# Revit family: BE_84292_de_DE
name_source: partatom
category: Leuchten
units: mm (PartAtom-declared; Revit-internal decimal feet)

## family parameters
Basisbauteil = Fläche
Beim Laden mit Abzugskörper schneiden = Ja
Bemaßung runder Anschluss = Durchmesser verwenden
Gemeinsam genutzt = Nein
Lichtquelle = Ja
Raumberechnungspunkt = Ja
Teiletyp = Normal

## types (6) — shared parameters
AC/DC = AC/DC
Aktualisierung = 2023-10-11T04:00:03
Anschlussleitung = 1.8 m 07RN8-F 5 G 1²
Beschreibung = Bodeneinbauleuchte
Beschreibung_Sonderanfertigung = Hier können Sie Informationen zur Sonderanfertigung eintragen.
CE_Konformität = ja
ENEC = ja
Einbaugehäuse = Nein
Einbautiefe = 220 mm
Energieeffizienzklasse = LED A++ - A
Farbfilter = 16777215
Farbtemperaturverschiebung bei Dämpfen der Lampe = <Keine Auswahl>
Farbwiedergabeindex = CRI > 80
Frequenz = 0/50-60 Hz
Gewicht = 5.35 kg
Hersteller = BEGA
Lampe = LED 16.8 W
Lastklassifizierung = Beleuchtung
Lebensdauerkriterien = L80B50 @ ta 25 °C = 160000 h
Logo = <Keine Auswahl>
Material_06 = BEGA_Oberfläche_Edelstahl_gebürstet
Material_09 = BEGA_Glas_klar
Material_10 = BEGA_Glas_matt
Material_13 = BEGA_Kunststoff_matt
Material_15 = BEGA_Leuchtmedium_matt
Material_17 = BEGA_Reflektor
Material_18 = BEGA_Gummi_schwarz
Neigungswinkel = 0.00°
Oberflächentemperatur = 30 °C
Produktdatenblatt = https://cdn.bega.com
Rutschhemmendes_Glas = ja
Scheinlast = 0 VA
Schutzart = IP 68...10m
Schutzklasse = I
Sonderanfertigung = Nein
Spannung = 240 V
URL = https://www.bega.com
Umgebungstemperatur = 25 °C
zero-valued in all types: Vorgabe-Ansicht

## per-type parameters (varying)
| type | Bestellnummer | Datei für fotometrisches Netz | Farbtemperatur | LED_Modulbezeichnung | Lampenlichtstrom | Leuchtenlichtstrom | Modell |
| BEGA_84292_R_K4 | 84292RK4 | BE_84292RK4.IES | 4000 | LED-0800/840 | 2920 lm | 2070 lm | 84292RK4 |
| BEGA_84292_K27 | 84292K27 | BE_84292K27.IES | 2700 | LED-0800/827 | 2715 lm | 1924 lm | 84292K27 |
| BEGA_84292_K3 | 84292K3 | BE_84292K3.IES | 3000 | LED-0800/830 | 2850 lm | 2020 lm | 84292K3 |
| BEGA_84292_K4 | 84292K4 | BE_84292K4.IES | 4000 | LED-0800/840 | 2920 lm | 2070 lm | 84292K4 |
| BEGA_84292_R_K27 | 84292RK27 | BE_84292RK27.IES | 2700 | LED-0800/827 | 2715 lm | 1924 lm | 84292RK27 |
| BEGA_84292_R_K3 | 84292RK3 | BE_84292RK3.IES | 3000 | LED-0800/830 | 2850 lm | 2020 lm | 84292RK3 |
